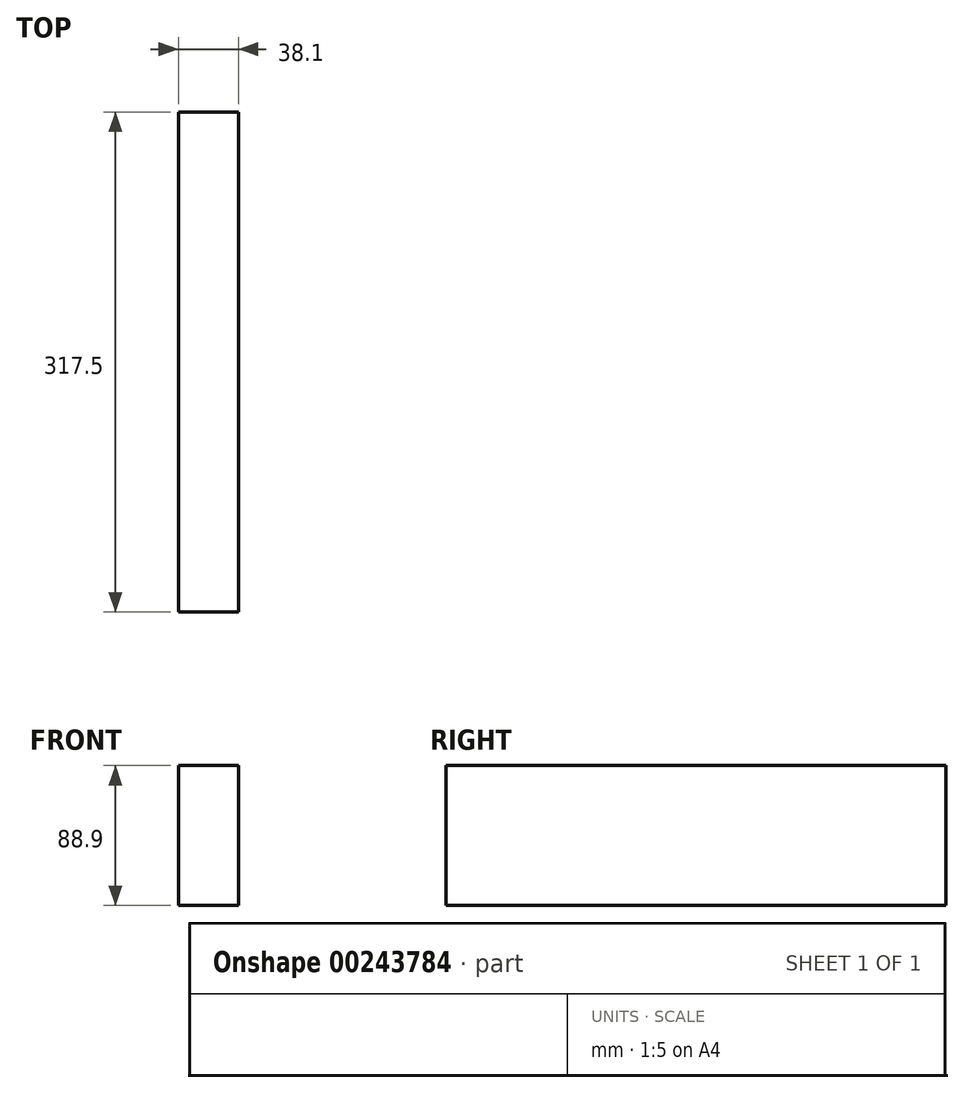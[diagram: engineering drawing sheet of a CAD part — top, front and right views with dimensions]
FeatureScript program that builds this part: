
annotation { "Feature Type Name" : "Feature", "Feature Type Description" : "" }
export const myFeature = defineFeature(function(context is Context, id is Id, definition is map)
    precondition{}
    {
        {
            var Q0;
            Q0=qCreatedBy(makeId("Front.planeOp"),FACE);
            var sketch = newSketch(context, id + "F0", { "sketchPlane" : qUnion([Q0])});
            skLineSegment(sketch, "E0.bottom", {"start": v(-81.67, 69.9) * mm, "end": v(-43.57, 69.9) * mm});
            skLineSegment(sketch, "E0.top", {"start": v(-81.67, -19) * mm, "end": v(-43.57, -19) * mm});
            skLineSegment(sketch, "E0.left", {"start": v(-81.67, 69.9) * mm, "end": v(-81.67, -19) * mm});
            skLineSegment(sketch, "E0.right", {"start": v(-43.57, 69.9) * mm, "end": v(-43.57, -19) * mm});
            skSolve(sketch);
        }
        {
            var Q0;
            Q0=makeQuery(id+"F0.imprint","IMPRINT",FACE,{"disambiguationData":[TD([[makeQuery(id+"F0.imprint","IMPRINT",EDGE,{"derivedFrom":sQuery(id+"F0.wireOp",EDGE,"E0.bottom")}),-1.0]])]});
            extrude(context, id + "F1", {"entities" : qUnion([Q0]), "depth" : 317.5 * mm});
        }
    });
